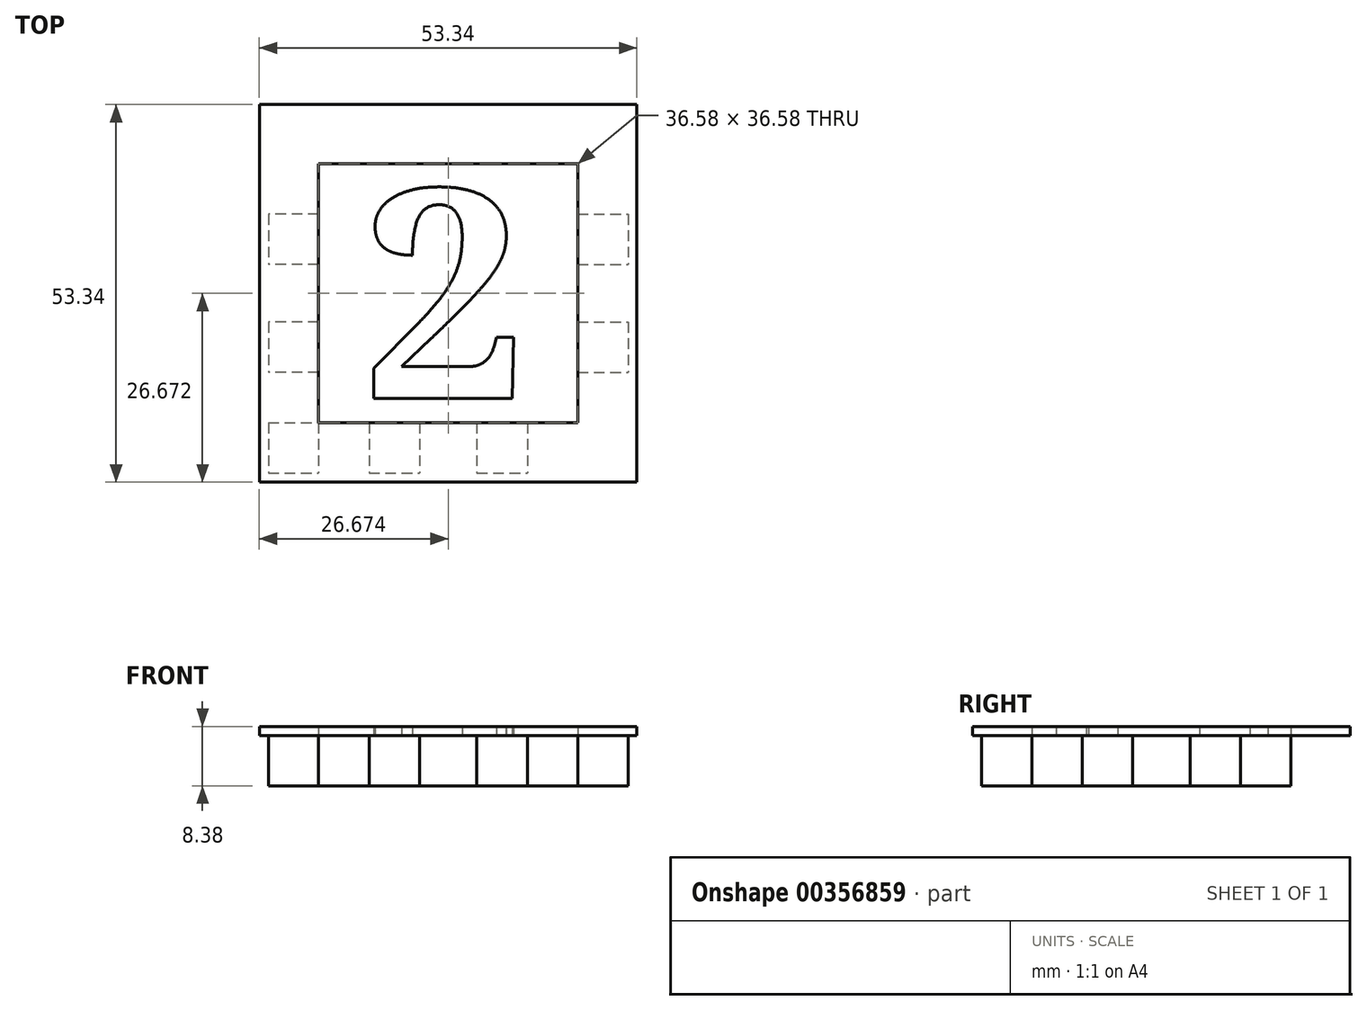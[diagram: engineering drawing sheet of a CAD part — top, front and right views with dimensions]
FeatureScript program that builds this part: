
annotation { "Feature Type Name" : "Feature", "Feature Type Description" : "" }
export const myFeature = defineFeature(function(context is Context, id is Id, definition is map)
    precondition{}
    {
        {
            var Q0;
            Q0=qCreatedBy(makeId("Top.planeOp"),FACE);
            var sketch = newSketch(context, id + "F0", { "sketchPlane" : qUnion([Q0])});
            skLineSegment(sketch, "E0.bottom", {"start": v(-28.29, 26.77) * mm, "end": v(15.4, 26.77) * mm});
            skLineSegment(sketch, "E0.top", {"start": v(-28.29, -24.03) * mm, "end": v(15.4, -24.03) * mm});
            skLineSegment(sketch, "E0.left", {"start": v(-28.29, 26.77) * mm, "end": v(-28.29, -24.03) * mm});
            skLineSegment(sketch, "E0.right", {"start": v(15.4, 26.77) * mm, "end": v(15.4, -24.03) * mm});
            skLineSegment(sketch, "E1.bottom", {"start": v(-28.29, 26.77) * mm, "end": v(-21.17, 26.77) * mm});
            skLineSegment(sketch, "E1.top", {"start": v(-28.29, 19.66) * mm, "end": v(-21.17, 19.66) * mm});
            skLineSegment(sketch, "E1.left", {"start": v(-28.29, 26.77) * mm, "end": v(-28.29, 19.66) * mm});
            skLineSegment(sketch, "E1.right", {"start": v(-21.17, 26.77) * mm, "end": v(-21.17, 19.66) * mm});
            skLineSegment(sketch, "E2.bottom", {"start": v(-21.17, 26.77) * mm, "end": v(-14.06, 26.77) * mm});
            skLineSegment(sketch, "E2.top", {"start": v(-21.17, 19.66) * mm, "end": v(-14.06, 19.66) * mm});
            skLineSegment(sketch, "E2.right", {"start": v(-14.06, 26.77) * mm, "end": v(-14.06, 19.66) * mm});
            skLineSegment(sketch, "E3.bottom", {"start": v(-14.06, 26.77) * mm, "end": v(-6.95, 26.77) * mm});
            skLineSegment(sketch, "E3.top", {"start": v(-14.06, 19.66) * mm, "end": v(-6.95, 19.66) * mm});
            skLineSegment(sketch, "E3.right", {"start": v(-6.95, 26.77) * mm, "end": v(-6.95, 19.66) * mm});
            skLineSegment(sketch, "E4.bottom", {"start": v(-6.95, 26.77) * mm, "end": v(1.18, 26.77) * mm});
            skLineSegment(sketch, "E4.top", {"start": v(-6.95, 19.66) * mm, "end": v(1.18, 19.66) * mm});
            skLineSegment(sketch, "E4.right", {"start": v(1.18, 26.77) * mm, "end": v(1.18, 19.66) * mm});
            skLineSegment(sketch, "E5.bottom", {"start": v(1.18, 26.77) * mm, "end": v(8.3, 26.77) * mm});
            skLineSegment(sketch, "E5.top", {"start": v(1.18, 19.66) * mm, "end": v(8.3, 19.66) * mm});
            skLineSegment(sketch, "E5.right", {"start": v(8.3, 26.77) * mm, "end": v(8.3, 19.66) * mm});
            skLineSegment(sketch, "E6.bottom", {"start": v(8.3, 26.77) * mm, "end": v(22.51, 26.77) * mm});
            skLineSegment(sketch, "E6.top", {"start": v(8.3, 19.66) * mm, "end": v(22.51, 19.66) * mm});
            skLineSegment(sketch, "E6.right", {"start": v(22.51, 26.77) * mm, "end": v(22.51, 19.66) * mm});
            skLineSegment(sketch, "E7.bottom", {"start": v(15.4, 26.77) * mm, "end": v(22.51, 26.77) * mm});
            skLineSegment(sketch, "E7.top", {"start": v(15.4, 19.66) * mm, "end": v(22.51, 19.66) * mm});
            skLineSegment(sketch, "E7.right", {"start": v(15.4, 26.77) * mm, "end": v(15.4, 19.66) * mm});
            skLineSegment(sketch, "E8.top", {"start": v(15.4, 12.55) * mm, "end": v(22.51, 12.55) * mm});
            skLineSegment(sketch, "E8.left", {"start": v(22.51, 19.66) * mm, "end": v(22.51, 12.55) * mm});
            skLineSegment(sketch, "E8.right", {"start": v(15.4, 19.66) * mm, "end": v(15.4, 12.55) * mm});
            skLineSegment(sketch, "E9.top", {"start": v(15.4, 5.44) * mm, "end": v(22.51, 5.44) * mm});
            skLineSegment(sketch, "E9.left", {"start": v(22.51, 12.55) * mm, "end": v(22.51, 5.44) * mm});
            skLineSegment(sketch, "E9.right", {"start": v(15.4, 12.55) * mm, "end": v(15.4, 5.44) * mm});
            skLineSegment(sketch, "E10.top", {"start": v(15.4, -2.7) * mm, "end": v(22.51, -2.7) * mm});
            skLineSegment(sketch, "E10.left", {"start": v(22.51, 5.44) * mm, "end": v(22.51, -2.7) * mm});
            skLineSegment(sketch, "E10.right", {"start": v(15.4, 5.44) * mm, "end": v(15.4, -2.7) * mm});
            skLineSegment(sketch, "E11.top", {"start": v(15.4, -9.8) * mm, "end": v(22.51, -9.8) * mm});
            skLineSegment(sketch, "E11.left", {"start": v(22.51, -2.7) * mm, "end": v(22.51, -9.8) * mm});
            skLineSegment(sketch, "E11.right", {"start": v(15.4, -2.7) * mm, "end": v(15.4, -9.8) * mm});
            skLineSegment(sketch, "E12.top", {"start": v(15.4, -16.92) * mm, "end": v(22.51, -16.92) * mm});
            skLineSegment(sketch, "E12.left", {"start": v(22.51, -9.8) * mm, "end": v(22.51, -16.92) * mm});
            skLineSegment(sketch, "E12.right", {"start": v(15.4, -9.8) * mm, "end": v(15.4, -16.92) * mm});
            skLineSegment(sketch, "E13.top", {"start": v(15.4, -24.03) * mm, "end": v(22.51, -24.03) * mm});
            skLineSegment(sketch, "E13.left", {"start": v(22.51, -16.92) * mm, "end": v(22.51, -24.03) * mm});
            skLineSegment(sketch, "E13.right", {"start": v(15.4, -16.92) * mm, "end": v(15.4, -24.03) * mm});
            skLineSegment(sketch, "E14.bottom", {"start": v(22.51, -16.92) * mm, "end": v(8.3, -16.92) * mm});
            skLineSegment(sketch, "E14.top", {"start": v(22.51, -24.03) * mm, "end": v(8.3, -24.03) * mm});
            skLineSegment(sketch, "E14.right", {"start": v(8.3, -16.92) * mm, "end": v(8.3, -24.03) * mm});
            skLineSegment(sketch, "E15.bottom", {"start": v(8.3, -16.92) * mm, "end": v(1.18, -16.92) * mm});
            skLineSegment(sketch, "E15.top", {"start": v(8.3, -24.03) * mm, "end": v(1.18, -24.03) * mm});
            skLineSegment(sketch, "E15.right", {"start": v(1.18, -16.92) * mm, "end": v(1.18, -24.03) * mm});
            skLineSegment(sketch, "E16.bottom", {"start": v(1.18, -16.92) * mm, "end": v(-6.95, -16.92) * mm});
            skLineSegment(sketch, "E16.top", {"start": v(1.18, -24.03) * mm, "end": v(-6.95, -24.03) * mm});
            skLineSegment(sketch, "E16.right", {"start": v(-6.95, -16.92) * mm, "end": v(-6.95, -24.03) * mm});
            skLineSegment(sketch, "E17.bottom", {"start": v(-6.95, -16.92) * mm, "end": v(-14.06, -16.92) * mm});
            skLineSegment(sketch, "E17.top", {"start": v(-6.95, -24.03) * mm, "end": v(-14.06, -24.03) * mm});
            skLineSegment(sketch, "E17.right", {"start": v(-14.06, -16.92) * mm, "end": v(-14.06, -24.03) * mm});
            skLineSegment(sketch, "E18.bottom", {"start": v(-21.17, 19.66) * mm, "end": v(-28.29, 19.66) * mm});
            skLineSegment(sketch, "E18.top", {"start": v(-21.17, 12.55) * mm, "end": v(-28.29, 12.55) * mm});
            skLineSegment(sketch, "E18.left", {"start": v(-21.17, 19.66) * mm, "end": v(-21.17, 12.55) * mm});
            skLineSegment(sketch, "E18.right", {"start": v(-28.29, 19.66) * mm, "end": v(-28.29, 12.55) * mm});
            skLineSegment(sketch, "E19.top", {"start": v(-21.17, 5.44) * mm, "end": v(-28.29, 5.44) * mm});
            skLineSegment(sketch, "E19.left", {"start": v(-21.17, 12.55) * mm, "end": v(-21.17, 5.44) * mm});
            skLineSegment(sketch, "E19.right", {"start": v(-28.29, 12.55) * mm, "end": v(-28.29, 5.44) * mm});
            skLineSegment(sketch, "E20.top", {"start": v(-21.17, -2.7) * mm, "end": v(-28.29, -2.7) * mm});
            skLineSegment(sketch, "E20.left", {"start": v(-21.17, 5.44) * mm, "end": v(-21.17, -2.7) * mm});
            skLineSegment(sketch, "E20.right", {"start": v(-28.29, 5.44) * mm, "end": v(-28.29, -2.7) * mm});
            skLineSegment(sketch, "E21.top", {"start": v(-21.17, -9.8) * mm, "end": v(-28.29, -9.8) * mm});
            skLineSegment(sketch, "E21.left", {"start": v(-21.17, -2.7) * mm, "end": v(-21.17, -9.8) * mm});
            skLineSegment(sketch, "E21.right", {"start": v(-28.29, -2.7) * mm, "end": v(-28.29, -9.8) * mm});
            skLineSegment(sketch, "E22.bottom", {"start": v(-28.29, -9.8) * mm, "end": v(-21.17, -9.8) * mm});
            skLineSegment(sketch, "E22.top", {"start": v(-28.29, -16.92) * mm, "end": v(-21.17, -16.92) * mm});
            skLineSegment(sketch, "E22.left", {"start": v(-28.29, -9.8) * mm, "end": v(-28.29, -16.92) * mm});
            skLineSegment(sketch, "E22.right", {"start": v(-21.17, -9.8) * mm, "end": v(-21.17, -16.92) * mm});
            skLineSegment(sketch, "E23.top", {"start": v(-28.29, -24.03) * mm, "end": v(-21.17, -24.03) * mm});
            skLineSegment(sketch, "E23.left", {"start": v(-28.29, -16.92) * mm, "end": v(-28.29, -24.03) * mm});
            skLineSegment(sketch, "E23.right", {"start": v(-21.17, -16.92) * mm, "end": v(-21.17, -24.03) * mm});
            skLineSegment(sketch, "E24.bottom", {"start": v(-21.17, -16.92) * mm, "end": v(-14.06, -16.92) * mm});
            skLineSegment(sketch, "E24.top", {"start": v(-21.17, -24.03) * mm, "end": v(-14.06, -24.03) * mm});
            skLineSegment(sketch, "E25.bottom", {"start": v(55.44, 26.09) * mm, "end": v(106.24, 26.09) * mm});
            skLineSegment(sketch, "E25.top", {"start": v(55.44, -24.71) * mm, "end": v(106.24, -24.71) * mm});
            skLineSegment(sketch, "E25.left", {"start": v(55.44, 26.09) * mm, "end": v(55.44, -24.71) * mm});
            skLineSegment(sketch, "E25.right", {"start": v(106.24, 26.09) * mm, "end": v(106.24, -24.71) * mm});
            skLineSegment(sketch, "E26.bottom", {"start": v(55.44, 26.09) * mm, "end": v(62.55, 26.09) * mm});
            skLineSegment(sketch, "E26.top", {"start": v(55.44, 18.97) * mm, "end": v(62.55, 18.97) * mm});
            skLineSegment(sketch, "E26.left", {"start": v(55.44, 26.09) * mm, "end": v(55.44, 18.97) * mm});
            skLineSegment(sketch, "E26.right", {"start": v(62.55, 26.09) * mm, "end": v(62.55, 18.97) * mm});
            skLineSegment(sketch, "E27.bottom", {"start": v(62.55, 26.09) * mm, "end": v(69.67, 26.09) * mm});
            skLineSegment(sketch, "E27.top", {"start": v(62.55, 18.97) * mm, "end": v(69.67, 18.97) * mm});
            skLineSegment(sketch, "E27.right", {"start": v(69.67, 26.09) * mm, "end": v(69.67, 18.97) * mm});
            skLineSegment(sketch, "E28.bottom", {"start": v(69.67, 26.09) * mm, "end": v(76.78, 26.09) * mm});
            skLineSegment(sketch, "E28.top", {"start": v(69.67, 18.97) * mm, "end": v(76.78, 18.97) * mm});
            skLineSegment(sketch, "E28.right", {"start": v(76.78, 26.09) * mm, "end": v(76.78, 18.97) * mm});
            skLineSegment(sketch, "E29.bottom", {"start": v(76.78, 26.09) * mm, "end": v(84.9, 26.09) * mm});
            skLineSegment(sketch, "E29.top", {"start": v(76.78, 18.97) * mm, "end": v(84.9, 18.97) * mm});
            skLineSegment(sketch, "E29.right", {"start": v(84.9, 26.09) * mm, "end": v(84.9, 18.97) * mm});
            skLineSegment(sketch, "E30.bottom", {"start": v(84.9, 26.09) * mm, "end": v(92.02, 26.09) * mm});
            skLineSegment(sketch, "E30.top", {"start": v(84.9, 18.97) * mm, "end": v(92.02, 18.97) * mm});
            skLineSegment(sketch, "E30.right", {"start": v(92.02, 26.09) * mm, "end": v(92.02, 18.97) * mm});
            skLineSegment(sketch, "E31.bottom", {"start": v(92.02, 26.09) * mm, "end": v(99.13, 26.09) * mm});
            skLineSegment(sketch, "E31.top", {"start": v(92.02, 18.97) * mm, "end": v(99.13, 18.97) * mm});
            skLineSegment(sketch, "E31.right", {"start": v(99.13, 26.09) * mm, "end": v(99.13, 18.97) * mm});
            skLineSegment(sketch, "E32.bottom", {"start": v(99.13, 26.09) * mm, "end": v(106.24, 26.09) * mm});
            skLineSegment(sketch, "E32.top", {"start": v(99.13, 18.97) * mm, "end": v(106.24, 18.97) * mm});
            skLineSegment(sketch, "E32.right", {"start": v(106.24, 26.09) * mm, "end": v(106.24, 18.97) * mm});
            skLineSegment(sketch, "E33.top", {"start": v(99.13, 11.86) * mm, "end": v(106.24, 11.86) * mm});
            skLineSegment(sketch, "E33.left", {"start": v(99.13, 18.97) * mm, "end": v(99.13, 11.86) * mm});
            skLineSegment(sketch, "E33.right", {"start": v(106.24, 18.97) * mm, "end": v(106.24, 11.86) * mm});
            skLineSegment(sketch, "E34.top", {"start": v(99.13, 4.75) * mm, "end": v(106.24, 4.75) * mm});
            skLineSegment(sketch, "E34.left", {"start": v(99.13, 11.86) * mm, "end": v(99.13, 4.75) * mm});
            skLineSegment(sketch, "E34.right", {"start": v(106.24, 11.86) * mm, "end": v(106.24, 4.75) * mm});
            skLineSegment(sketch, "E35.top", {"start": v(99.13, -3.38) * mm, "end": v(106.24, -3.38) * mm});
            skLineSegment(sketch, "E35.left", {"start": v(99.13, 4.75) * mm, "end": v(99.13, -3.38) * mm});
            skLineSegment(sketch, "E35.right", {"start": v(106.24, 4.75) * mm, "end": v(106.24, -3.38) * mm});
            skLineSegment(sketch, "E36.top", {"start": v(99.13, -10.49) * mm, "end": v(106.24, -10.49) * mm});
            skLineSegment(sketch, "E36.left", {"start": v(99.13, -3.38) * mm, "end": v(99.13, -10.49) * mm});
            skLineSegment(sketch, "E36.right", {"start": v(106.24, -3.38) * mm, "end": v(106.24, -10.49) * mm});
            skLineSegment(sketch, "E37.top", {"start": v(99.13, -17.6) * mm, "end": v(106.24, -17.6) * mm});
            skLineSegment(sketch, "E37.left", {"start": v(99.13, -10.49) * mm, "end": v(99.13, -17.6) * mm});
            skLineSegment(sketch, "E37.right", {"start": v(106.24, -10.49) * mm, "end": v(106.24, -17.6) * mm});
            skLineSegment(sketch, "E38.top", {"start": v(99.13, -24.71) * mm, "end": v(106.24, -24.71) * mm});
            skLineSegment(sketch, "E38.left", {"start": v(99.13, -17.6) * mm, "end": v(99.13, -24.71) * mm});
            skLineSegment(sketch, "E38.right", {"start": v(106.24, -17.6) * mm, "end": v(106.24, -24.71) * mm});
            skLineSegment(sketch, "E39.bottom", {"start": v(99.13, -17.6) * mm, "end": v(92.02, -17.6) * mm});
            skLineSegment(sketch, "E39.top", {"start": v(99.13, -24.71) * mm, "end": v(92.02, -24.71) * mm});
            skLineSegment(sketch, "E39.right", {"start": v(92.02, -17.6) * mm, "end": v(92.02, -24.71) * mm});
            skLineSegment(sketch, "E40.bottom", {"start": v(92.02, -17.6) * mm, "end": v(84.9, -17.6) * mm});
            skLineSegment(sketch, "E40.top", {"start": v(92.02, -24.71) * mm, "end": v(84.9, -24.71) * mm});
            skLineSegment(sketch, "E40.right", {"start": v(84.9, -17.6) * mm, "end": v(84.9, -24.71) * mm});
            skLineSegment(sketch, "E41.bottom", {"start": v(84.9, -17.6) * mm, "end": v(76.78, -17.6) * mm});
            skLineSegment(sketch, "E41.top", {"start": v(84.9, -24.71) * mm, "end": v(76.78, -24.71) * mm});
            skLineSegment(sketch, "E41.right", {"start": v(76.78, -17.6) * mm, "end": v(76.78, -24.71) * mm});
            skLineSegment(sketch, "E42.bottom", {"start": v(76.78, -17.6) * mm, "end": v(69.67, -17.6) * mm});
            skLineSegment(sketch, "E42.top", {"start": v(76.78, -24.71) * mm, "end": v(69.67, -24.71) * mm});
            skLineSegment(sketch, "E42.right", {"start": v(69.67, -17.6) * mm, "end": v(69.67, -24.71) * mm});
            skLineSegment(sketch, "E43.bottom", {"start": v(62.55, 18.97) * mm, "end": v(55.44, 18.97) * mm});
            skLineSegment(sketch, "E43.top", {"start": v(62.55, 11.86) * mm, "end": v(55.44, 11.86) * mm});
            skLineSegment(sketch, "E43.left", {"start": v(62.55, 18.97) * mm, "end": v(62.55, 11.86) * mm});
            skLineSegment(sketch, "E43.right", {"start": v(55.44, 18.97) * mm, "end": v(55.44, 11.86) * mm});
            skLineSegment(sketch, "E44.top", {"start": v(62.55, 4.75) * mm, "end": v(55.44, 4.75) * mm});
            skLineSegment(sketch, "E44.left", {"start": v(62.55, 11.86) * mm, "end": v(62.55, 4.75) * mm});
            skLineSegment(sketch, "E44.right", {"start": v(55.44, 11.86) * mm, "end": v(55.44, 4.75) * mm});
            skLineSegment(sketch, "E45.top", {"start": v(62.55, -3.38) * mm, "end": v(55.44, -3.38) * mm});
            skLineSegment(sketch, "E45.left", {"start": v(62.55, 4.75) * mm, "end": v(62.55, -3.38) * mm});
            skLineSegment(sketch, "E45.right", {"start": v(55.44, 4.75) * mm, "end": v(55.44, -3.38) * mm});
            skLineSegment(sketch, "E46.top", {"start": v(62.55, -10.49) * mm, "end": v(55.44, -10.49) * mm});
            skLineSegment(sketch, "E46.left", {"start": v(62.55, -3.38) * mm, "end": v(62.55, -10.49) * mm});
            skLineSegment(sketch, "E46.right", {"start": v(55.44, -3.38) * mm, "end": v(55.44, -10.49) * mm});
            skLineSegment(sketch, "E47.top", {"start": v(62.55, -17.6) * mm, "end": v(55.44, -17.6) * mm});
            skLineSegment(sketch, "E47.left", {"start": v(62.55, -10.49) * mm, "end": v(62.55, -17.6) * mm});
            skLineSegment(sketch, "E47.right", {"start": v(55.44, -10.49) * mm, "end": v(55.44, -17.6) * mm});
            skLineSegment(sketch, "E48.bottom", {"start": v(62.55, -17.6) * mm, "end": v(69.67, -17.6) * mm});
            skLineSegment(sketch, "E48.top", {"start": v(62.55, -24.71) * mm, "end": v(69.67, -24.71) * mm});
            skLineSegment(sketch, "E48.left", {"start": v(62.55, -17.6) * mm, "end": v(62.55, -24.71) * mm});
            skLineSegment(sketch, "E49.top", {"start": v(62.55, -24.71) * mm, "end": v(55.44, -24.71) * mm});
            skLineSegment(sketch, "E49.right", {"start": v(55.44, -17.6) * mm, "end": v(55.44, -24.71) * mm});
            skSolve(sketch);
        }
        {
            var Q0;
            Q0=makeQuery(id+"F0.imprint","IMPRINT",FACE,{"disambiguationData":[TD([[makeQuery(id+"F0.imprint","IMPRINT",EDGE,{"derivedFrom":sQuery(id+"F0.wireOp",EDGE,"E1.bottom")}),-1.0]])]});
            var Q1;
            Q1=makeQuery(id+"F0.imprint","IMPRINT",FACE,{"disambiguationData":[TD([[makeQuery(id+"F0.imprint","IMPRINT",EDGE,{"derivedFrom":sQuery(id+"F0.wireOp",EDGE,"E3.bottom")}),-1.0]])]});
            var Q2;
            Q2=makeQuery(id+"F0.imprint","IMPRINT",FACE,{"disambiguationData":[TD([[makeQuery(id+"F0.imprint","IMPRINT",EDGE,{"derivedFrom":sQuery(id+"F0.wireOp",EDGE,"E5.bottom")}),-1.0]])]});
            var Q3;
            Q3=makeQuery(id+"F0.imprint","IMPRINT",FACE,{"disambiguationData":[TD([[makeQuery(id+"F0.imprint","IMPRINT",EDGE,{"derivedFrom":sQuery(id+"F0.wireOp",EDGE,"E7.bottom")}),-1.0]])]});
            var Q4;
            Q4=makeQuery(id+"F0.imprint","IMPRINT",FACE,{"disambiguationData":[TD([[makeQuery(id+"F0.imprint","IMPRINT",EDGE,{"derivedFrom":sQuery(id+"F0.wireOp",EDGE,"E8.top")}),-1.0]])]});
            var Q5;
            Q5=makeQuery(id+"F0.imprint","IMPRINT",FACE,{"disambiguationData":[TD([[makeQuery(id+"F0.imprint","IMPRINT",EDGE,{"derivedFrom":sQuery(id+"F0.wireOp",EDGE,"E10.top")}),-1.0]])]});
            var Q6;
            {var subQ0=sQuery(id+"F0.wireOp",EDGE,"E13.right");Q6=makeQuery(id+"F0.imprint","IMPRINT",FACE,{"disambiguationData":[TD([[makeQuery(id+"F0.imprint","IMPRINT",EDGE,{"derivedFrom":subQ0}),1.0]])]});}
            var Q7;
            Q7=makeQuery(id+"F0.imprint","IMPRINT",FACE,{"disambiguationData":[TD([[makeQuery(id+"F0.imprint","IMPRINT",EDGE,{"derivedFrom":sQuery(id+"F0.wireOp",EDGE,"E15.bottom")}),1.0]])]});
            var Q8;
            Q8=makeQuery(id+"F0.imprint","IMPRINT",FACE,{"disambiguationData":[TD([[makeQuery(id+"F0.imprint","IMPRINT",EDGE,{"derivedFrom":sQuery(id+"F0.wireOp",EDGE,"E2.top")}),-1.0]])]});
            var Q9;
            Q9=makeQuery(id+"F0.imprint","IMPRINT",FACE,{"disambiguationData":[TD([[makeQuery(id+"F0.imprint","IMPRINT",EDGE,{"derivedFrom":sQuery(id+"F0.wireOp",EDGE,"E17.bottom")}),1.0]])]});
            var Q10;
            Q10=makeQuery(id+"F0.imprint","IMPRINT",FACE,{"disambiguationData":[TD([[makeQuery(id+"F0.imprint","IMPRINT",EDGE,{"derivedFrom":sQuery(id+"F0.wireOp",EDGE,"E22.top")}),-1.0]])]});
            var Q11;
            Q11=makeQuery(id+"F0.imprint","IMPRINT",FACE,{"disambiguationData":[TD([[makeQuery(id+"F0.imprint","IMPRINT",EDGE,{"derivedFrom":sQuery(id+"F0.wireOp",EDGE,"E20.top")}),1.0]])]});
            var Q12;
            Q12=makeQuery(id+"F0.imprint","IMPRINT",FACE,{"disambiguationData":[TD([[makeQuery(id+"F0.imprint","IMPRINT",EDGE,{"derivedFrom":sQuery(id+"F0.wireOp",EDGE,"E18.top")}),1.0]])]});
            var Q13;
            Q13=makeQuery(id+"F0.imprint","IMPRINT",FACE,{"disambiguationData":[TD([[makeQuery(id+"F0.imprint","IMPRINT",EDGE,{"derivedFrom":sQuery(id+"F0.wireOp",EDGE,"E27.top")}),-1.0]])]});
            var Q14;
            Q14=makeQuery(id+"F0.imprint","IMPRINT",FACE,{"disambiguationData":[TD([[makeQuery(id+"F0.imprint","IMPRINT",EDGE,{"derivedFrom":sQuery(id+"F0.wireOp",EDGE,"E31.bottom")}),-1.0]])]});
            var Q15;
            Q15=makeQuery(id+"F0.imprint","IMPRINT",FACE,{"disambiguationData":[TD([[makeQuery(id+"F0.imprint","IMPRINT",EDGE,{"derivedFrom":sQuery(id+"F0.wireOp",EDGE,"E29.bottom")}),-1.0]])]});
            var Q16;
            Q16=makeQuery(id+"F0.imprint","IMPRINT",FACE,{"disambiguationData":[TD([[makeQuery(id+"F0.imprint","IMPRINT",EDGE,{"derivedFrom":sQuery(id+"F0.wireOp",EDGE,"E43.bottom")}),1.0]])]});
            var Q17;
            Q17=makeQuery(id+"F0.imprint","IMPRINT",FACE,{"disambiguationData":[TD([[makeQuery(id+"F0.imprint","IMPRINT",EDGE,{"derivedFrom":sQuery(id+"F0.wireOp",EDGE,"E44.top")}),1.0]])]});
            var Q18;
            Q18=makeQuery(id+"F0.imprint","IMPRINT",FACE,{"disambiguationData":[TD([[makeQuery(id+"F0.imprint","IMPRINT",EDGE,{"derivedFrom":sQuery(id+"F0.wireOp",EDGE,"E36.top")}),-1.0]])]});
            var Q19;
            Q19=makeQuery(id+"F0.imprint","IMPRINT",FACE,{"disambiguationData":[TD([[makeQuery(id+"F0.imprint","IMPRINT",EDGE,{"derivedFrom":sQuery(id+"F0.wireOp",EDGE,"E34.top")}),-1.0]])]});
            var Q20;
            Q20=makeQuery(id+"F0.imprint","IMPRINT",FACE,{"disambiguationData":[TD([[makeQuery(id+"F0.imprint","IMPRINT",EDGE,{"derivedFrom":sQuery(id+"F0.wireOp",EDGE,"E46.top")}),1.0]])]});
            var Q21;
            Q21=makeQuery(id+"F0.imprint","IMPRINT",FACE,{"disambiguationData":[TD([[makeQuery(id+"F0.imprint","IMPRINT",EDGE,{"derivedFrom":sQuery(id+"F0.wireOp",EDGE,"E32.top")}),-1.0]])]});
            var Q22;
            Q22=makeQuery(id+"F0.imprint","IMPRINT",FACE,{"disambiguationData":[TD([[makeQuery(id+"F0.imprint","IMPRINT",EDGE,{"derivedFrom":sQuery(id+"F0.wireOp",EDGE,"E27.bottom")}),-1.0]])]});
            var Q23;
            Q23=makeQuery(id+"F0.imprint","IMPRINT",FACE,{"disambiguationData":[TD([[makeQuery(id+"F0.imprint","IMPRINT",EDGE,{"derivedFrom":sQuery(id+"F0.wireOp",EDGE,"E42.bottom")}),1.0]])]});
            var Q24;
            Q24=makeQuery(id+"F0.imprint","IMPRINT",FACE,{"disambiguationData":[TD([[makeQuery(id+"F0.imprint","IMPRINT",EDGE,{"derivedFrom":sQuery(id+"F0.wireOp",EDGE,"E40.bottom")}),1.0]])]});
            extrude(context, id + "F1", {"entities" : qUnion([Q0, Q1, Q2, Q3, Q4, Q5, Q6, Q7, Q8, Q9, Q10, Q11, Q12, Q13, Q14, Q15, Q16, Q17, Q18, Q19, Q20, Q21, Q22, Q23, Q24]), "depth" : 7.11 * mm});
        }
        {
            var Q0;
            Q0=makeQuery(id+"F1.opExtrude","CAP_FACE",FACE,{"disambiguationData":[OSD([sQuery(id+"F0.wireOp",EDGE,"E2.top"),sQuery(id+"F0.wireOp",EDGE,"E3.bottom"),sQuery(id+"F0.wireOp",EDGE,"E2.right"),sQuery(id+"F0.wireOp",EDGE,"E4.top"),sQuery(id+"F0.wireOp",EDGE,"E3.right"),sQuery(id+"F0.wireOp",EDGE,"E5.bottom"),sQuery(id+"F0.wireOp",EDGE,"E4.right"),sQuery(id+"F0.wireOp",EDGE,"E6.top"),sQuery(id+"F0.wireOp",EDGE,"E5.right"),sQuery(id+"F0.wireOp",EDGE,"E8.right"),sQuery(id+"F0.wireOp",EDGE,"E8.top"),sQuery(id+"F0.wireOp",EDGE,"E9.left"),sQuery(id+"F0.wireOp",EDGE,"E9.top"),sQuery(id+"F0.wireOp",EDGE,"E10.right"),sQuery(id+"F0.wireOp",EDGE,"E10.top"),sQuery(id+"F0.wireOp",EDGE,"E11.left"),sQuery(id+"F0.wireOp",EDGE,"E11.top"),sQuery(id+"F0.wireOp",EDGE,"E12.right"),sQuery(id+"F0.wireOp",EDGE,"E14.bottom"),sQuery(id+"F0.wireOp",EDGE,"E15.top"),sQuery(id+"F0.wireOp",EDGE,"E14.right"),sQuery(id+"F0.wireOp",EDGE,"E16.bottom"),sQuery(id+"F0.wireOp",EDGE,"E15.right"),sQuery(id+"F0.wireOp",EDGE,"E17.top"),sQuery(id+"F0.wireOp",EDGE,"E16.right"),sQuery(id+"F0.wireOp",EDGE,"E18.left"),sQuery(id+"F0.wireOp",EDGE,"E18.top"),sQuery(id+"F0.wireOp",EDGE,"E19.right"),sQuery(id+"F0.wireOp",EDGE,"E19.top"),sQuery(id+"F0.wireOp",EDGE,"E20.left"),sQuery(id+"F0.wireOp",EDGE,"E20.top"),sQuery(id+"F0.wireOp",EDGE,"E21.right"),sQuery(id+"F0.wireOp",EDGE,"E22.bottom"),sQuery(id+"F0.wireOp",EDGE,"E22.right"),sQuery(id+"F0.wireOp",EDGE,"E24.bottom"),sQuery(id+"F0.wireOp",EDGE,"E17.right")])],"isStart":false});
            var sketch = newSketch(context, id + "F2", { "sketchPlane" : qUnion([Q0])});
            skLineSegment(sketch, "E50.bottom", {"start": v(-29.56, -25.3) * mm, "end": v(23.78, -25.3) * mm});
            skLineSegment(sketch, "E50.top", {"start": v(-29.56, -16.92) * mm, "end": v(23.78, -16.92) * mm});
            skLineSegment(sketch, "E50.left", {"start": v(-29.56, -25.3) * mm, "end": v(-29.56, -16.92) * mm});
            skLineSegment(sketch, "E50.right", {"start": v(23.78, -25.3) * mm, "end": v(23.78, -16.92) * mm});
            skLineSegment(sketch, "E51.bottom", {"start": v(-29.56, -25.3) * mm, "end": v(-21.17, -25.3) * mm});
            skLineSegment(sketch, "E51.top", {"start": v(-29.56, 28.04) * mm, "end": v(-21.17, 28.04) * mm});
            skLineSegment(sketch, "E51.left", {"start": v(-29.56, -25.3) * mm, "end": v(-29.56, 28.04) * mm});
            skLineSegment(sketch, "E51.right", {"start": v(-21.17, -25.3) * mm, "end": v(-21.17, 28.04) * mm});
            skLineSegment(sketch, "E52.bottom", {"start": v(-29.56, 19.66) * mm, "end": v(23.78, 19.66) * mm});
            skLineSegment(sketch, "E52.top", {"start": v(-29.56, 28.04) * mm, "end": v(23.78, 28.04) * mm});
            skLineSegment(sketch, "E52.left", {"start": v(-29.56, 19.66) * mm, "end": v(-29.56, 28.04) * mm});
            skLineSegment(sketch, "E52.right", {"start": v(23.78, 19.66) * mm, "end": v(23.78, 28.04) * mm});
            skLineSegment(sketch, "E53.bottom", {"start": v(23.78, 28.04) * mm, "end": v(15.4, 28.04) * mm});
            skLineSegment(sketch, "E53.top", {"start": v(23.78, -25.3) * mm, "end": v(15.4, -25.3) * mm});
            skLineSegment(sketch, "E53.left", {"start": v(23.78, 28.04) * mm, "end": v(23.78, -25.3) * mm});
            skLineSegment(sketch, "E53.right", {"start": v(15.4, 28.04) * mm, "end": v(15.4, -25.3) * mm});
            skSolve(sketch);
        }
        {
            var Q0;
            Q0=qSketchRegion(id+"F2",true);
            extrude(context, id + "F3", {"entities" : qUnion([Q0]), "depth" : 1.27 * mm});
        }
        {
            var Q0;
            Q0=makeQuery(id+"F1.opExtrude","CAP_FACE",FACE,{"disambiguationData":[OSD([sQuery(id+"F0.wireOp",EDGE,"E27.bottom"),sQuery(id+"F0.wireOp",EDGE,"E26.right"),sQuery(id+"F0.wireOp",EDGE,"E28.top"),sQuery(id+"F0.wireOp",EDGE,"E27.right"),sQuery(id+"F0.wireOp",EDGE,"E29.bottom"),sQuery(id+"F0.wireOp",EDGE,"E28.right"),sQuery(id+"F0.wireOp",EDGE,"E30.top"),sQuery(id+"F0.wireOp",EDGE,"E29.right"),sQuery(id+"F0.wireOp",EDGE,"E31.bottom"),sQuery(id+"F0.wireOp",EDGE,"E30.right"),sQuery(id+"F0.wireOp",EDGE,"E31.right"),sQuery(id+"F0.wireOp",EDGE,"E32.top"),sQuery(id+"F0.wireOp",EDGE,"E33.right"),sQuery(id+"F0.wireOp",EDGE,"E33.top"),sQuery(id+"F0.wireOp",EDGE,"E34.left"),sQuery(id+"F0.wireOp",EDGE,"E34.top"),sQuery(id+"F0.wireOp",EDGE,"E35.right"),sQuery(id+"F0.wireOp",EDGE,"E35.top"),sQuery(id+"F0.wireOp",EDGE,"E36.left"),sQuery(id+"F0.wireOp",EDGE,"E36.top"),sQuery(id+"F0.wireOp",EDGE,"E37.right"),sQuery(id+"F0.wireOp",EDGE,"E37.top"),sQuery(id+"F0.wireOp",EDGE,"E39.bottom"),sQuery(id+"F0.wireOp",EDGE,"E40.top"),sQuery(id+"F0.wireOp",EDGE,"E39.right"),sQuery(id+"F0.wireOp",EDGE,"E41.bottom"),sQuery(id+"F0.wireOp",EDGE,"E40.right"),sQuery(id+"F0.wireOp",EDGE,"E42.top"),sQuery(id+"F0.wireOp",EDGE,"E41.right"),sQuery(id+"F0.wireOp",EDGE,"E43.bottom"),sQuery(id+"F0.wireOp",EDGE,"E43.right"),sQuery(id+"F0.wireOp",EDGE,"E43.top"),sQuery(id+"F0.wireOp",EDGE,"E44.left"),sQuery(id+"F0.wireOp",EDGE,"E44.top"),sQuery(id+"F0.wireOp",EDGE,"E45.right"),sQuery(id+"F0.wireOp",EDGE,"E45.top"),sQuery(id+"F0.wireOp",EDGE,"E46.left"),sQuery(id+"F0.wireOp",EDGE,"E46.top"),sQuery(id+"F0.wireOp",EDGE,"E47.right"),sQuery(id+"F0.wireOp",EDGE,"E48.bottom"),sQuery(id+"F0.wireOp",EDGE,"E42.right"),sQuery(id+"F0.wireOp",EDGE,"E47.top")])],"isStart":false});
            var sketch = newSketch(context, id + "F4", { "sketchPlane" : qUnion([Q0])});
            skLineSegment(sketch, "E54.bottom", {"start": v(55.44, -24.71) * mm, "end": v(62.55, -24.71) * mm});
            skLineSegment(sketch, "E54.top", {"start": v(55.44, 26.09) * mm, "end": v(62.55, 26.09) * mm});
            skLineSegment(sketch, "E54.left", {"start": v(55.44, -24.71) * mm, "end": v(55.44, 26.09) * mm});
            skLineSegment(sketch, "E54.right", {"start": v(62.55, -24.71) * mm, "end": v(62.55, 26.09) * mm});
            skLineSegment(sketch, "E55.bottom", {"start": v(55.44, -24.71) * mm, "end": v(106.24, -24.71) * mm});
            skLineSegment(sketch, "E55.top", {"start": v(55.44, -17.6) * mm, "end": v(106.24, -17.6) * mm});
            skLineSegment(sketch, "E55.left", {"start": v(55.44, -24.71) * mm, "end": v(55.44, -17.6) * mm});
            skLineSegment(sketch, "E55.right", {"start": v(106.24, -24.71) * mm, "end": v(106.24, -17.6) * mm});
            skLineSegment(sketch, "E56.bottom", {"start": v(106.24, -24.71) * mm, "end": v(99.13, -24.71) * mm});
            skLineSegment(sketch, "E56.top", {"start": v(106.24, 26.09) * mm, "end": v(99.13, 26.09) * mm});
            skLineSegment(sketch, "E56.left", {"start": v(106.24, -24.71) * mm, "end": v(106.24, 26.09) * mm});
            skLineSegment(sketch, "E56.right", {"start": v(99.13, -24.71) * mm, "end": v(99.13, 26.09) * mm});
            skLineSegment(sketch, "E57.bottom", {"start": v(106.24, 26.09) * mm, "end": v(55.44, 26.09) * mm});
            skLineSegment(sketch, "E57.top", {"start": v(106.24, 18.97) * mm, "end": v(55.44, 18.97) * mm});
            skLineSegment(sketch, "E57.left", {"start": v(106.24, 26.09) * mm, "end": v(106.24, 18.97) * mm});
            skLineSegment(sketch, "E57.right", {"start": v(55.44, 26.09) * mm, "end": v(55.44, 18.97) * mm});
            skSolve(sketch);
        }
        {
            var Q0;
            Q0=qSketchRegion(id+"F4",true);
            extrude(context, id + "F5", {"entities" : qUnion([Q0]), "depth" : 1.27 * mm});
        }
        {
            var Q0;
            Q0=makeQuery(id+"F1.opExtrude","SWEPT_BODY",BODY,{"disambiguationData":[OSD([sQuery(id+"F0.wireOp",EDGE,"E27.bottom"),sQuery(id+"F0.wireOp",EDGE,"E26.right"),sQuery(id+"F0.wireOp",EDGE,"E28.top"),sQuery(id+"F0.wireOp",EDGE,"E27.right"),sQuery(id+"F0.wireOp",EDGE,"E29.bottom"),sQuery(id+"F0.wireOp",EDGE,"E28.right"),sQuery(id+"F0.wireOp",EDGE,"E30.top"),sQuery(id+"F0.wireOp",EDGE,"E29.right"),sQuery(id+"F0.wireOp",EDGE,"E31.bottom"),sQuery(id+"F0.wireOp",EDGE,"E30.right"),sQuery(id+"F0.wireOp",EDGE,"E31.right"),sQuery(id+"F0.wireOp",EDGE,"E32.top"),sQuery(id+"F0.wireOp",EDGE,"E33.right"),sQuery(id+"F0.wireOp",EDGE,"E33.top"),sQuery(id+"F0.wireOp",EDGE,"E34.left"),sQuery(id+"F0.wireOp",EDGE,"E34.top"),sQuery(id+"F0.wireOp",EDGE,"E35.right"),sQuery(id+"F0.wireOp",EDGE,"E35.top"),sQuery(id+"F0.wireOp",EDGE,"E36.left"),sQuery(id+"F0.wireOp",EDGE,"E36.top"),sQuery(id+"F0.wireOp",EDGE,"E37.right"),sQuery(id+"F0.wireOp",EDGE,"E37.top"),sQuery(id+"F0.wireOp",EDGE,"E39.bottom"),sQuery(id+"F0.wireOp",EDGE,"E40.top"),sQuery(id+"F0.wireOp",EDGE,"E39.right"),sQuery(id+"F0.wireOp",EDGE,"E41.bottom"),sQuery(id+"F0.wireOp",EDGE,"E40.right"),sQuery(id+"F0.wireOp",EDGE,"E42.top"),sQuery(id+"F0.wireOp",EDGE,"E41.right"),sQuery(id+"F0.wireOp",EDGE,"E43.bottom"),sQuery(id+"F0.wireOp",EDGE,"E43.right"),sQuery(id+"F0.wireOp",EDGE,"E43.top"),sQuery(id+"F0.wireOp",EDGE,"E44.left"),sQuery(id+"F0.wireOp",EDGE,"E44.top"),sQuery(id+"F0.wireOp",EDGE,"E45.right"),sQuery(id+"F0.wireOp",EDGE,"E45.top"),sQuery(id+"F0.wireOp",EDGE,"E46.left"),sQuery(id+"F0.wireOp",EDGE,"E46.top"),sQuery(id+"F0.wireOp",EDGE,"E47.right"),sQuery(id+"F0.wireOp",EDGE,"E48.bottom"),sQuery(id+"F0.wireOp",EDGE,"E42.right"),sQuery(id+"F0.wireOp",EDGE,"E47.top")])]});
            var Q1;
            Q1=makeQuery(id+"F5.opExtrude","SWEPT_BODY",BODY,{"disambiguationData":[OSD([sQuery(id+"F4.wireOp",EDGE,"E54.left"),sQuery(id+"F4.wireOp",EDGE,"E54.right"),sQuery(id+"F4.wireOp",EDGE,"E55.bottom"),sQuery(id+"F4.wireOp",EDGE,"E55.top"),sQuery(id+"F4.wireOp",EDGE,"E55.left"),sQuery(id+"F4.wireOp",EDGE,"E56.bottom"),sQuery(id+"F4.wireOp",EDGE,"E56.left"),sQuery(id+"F4.wireOp",EDGE,"E56.right"),sQuery(id+"F4.wireOp",EDGE,"E57.bottom"),sQuery(id+"F4.wireOp",EDGE,"E57.top"),sQuery(id+"F4.wireOp",EDGE,"E57.left"),sQuery(id+"F4.wireOp",EDGE,"E57.right")])]});
            deleteBodies(context, id + "F6", {"entities" : qUnion([Q0, Q1])});
        }
        {
            var Q0;
            Q0=makeQuery(id+"F1.opExtrude","CAP_FACE",FACE,{"disambiguationData":[OSD([sQuery(id+"F0.wireOp",EDGE,"E2.top"),sQuery(id+"F0.wireOp",EDGE,"E3.bottom"),sQuery(id+"F0.wireOp",EDGE,"E2.right"),sQuery(id+"F0.wireOp",EDGE,"E4.top"),sQuery(id+"F0.wireOp",EDGE,"E3.right"),sQuery(id+"F0.wireOp",EDGE,"E5.bottom"),sQuery(id+"F0.wireOp",EDGE,"E4.right"),sQuery(id+"F0.wireOp",EDGE,"E6.top"),sQuery(id+"F0.wireOp",EDGE,"E5.right"),sQuery(id+"F0.wireOp",EDGE,"E8.right"),sQuery(id+"F0.wireOp",EDGE,"E8.top"),sQuery(id+"F0.wireOp",EDGE,"E9.left"),sQuery(id+"F0.wireOp",EDGE,"E9.top"),sQuery(id+"F0.wireOp",EDGE,"E10.right"),sQuery(id+"F0.wireOp",EDGE,"E10.top"),sQuery(id+"F0.wireOp",EDGE,"E11.left"),sQuery(id+"F0.wireOp",EDGE,"E11.top"),sQuery(id+"F0.wireOp",EDGE,"E12.right"),sQuery(id+"F0.wireOp",EDGE,"E14.bottom"),sQuery(id+"F0.wireOp",EDGE,"E15.top"),sQuery(id+"F0.wireOp",EDGE,"E14.right"),sQuery(id+"F0.wireOp",EDGE,"E16.bottom"),sQuery(id+"F0.wireOp",EDGE,"E15.right"),sQuery(id+"F0.wireOp",EDGE,"E17.top"),sQuery(id+"F0.wireOp",EDGE,"E16.right"),sQuery(id+"F0.wireOp",EDGE,"E18.left"),sQuery(id+"F0.wireOp",EDGE,"E18.top"),sQuery(id+"F0.wireOp",EDGE,"E19.right"),sQuery(id+"F0.wireOp",EDGE,"E19.top"),sQuery(id+"F0.wireOp",EDGE,"E20.left"),sQuery(id+"F0.wireOp",EDGE,"E20.top"),sQuery(id+"F0.wireOp",EDGE,"E21.right"),sQuery(id+"F0.wireOp",EDGE,"E22.bottom"),sQuery(id+"F0.wireOp",EDGE,"E22.right"),sQuery(id+"F0.wireOp",EDGE,"E24.bottom"),sQuery(id+"F0.wireOp",EDGE,"E17.right")])],"isStart":false});
            var sketch = newSketch(context, id + "F7", { "sketchPlane" : qUnion([Q0])});
            skText(sketch, "E58", { "text": "2", "fontName": "NotoSerif-Bold.ttf"});
            const initialGuessF7  = {"E58": [-0.01482, -0.0135, 1, 0, 0.02974]};
            skSetInitialGuess(sketch, initialGuessF7);
            skSolve(sketch);
        }
        {
            var Q0;
            Q0 = qSketchRegion(id + "F7", true);
            extrude(context, id + "F8", {"entities" : qUnion([Q0]), "operationType" : NewBodyOperationType.ADD, "depth" : 1.27 * mm});
        }
    });
